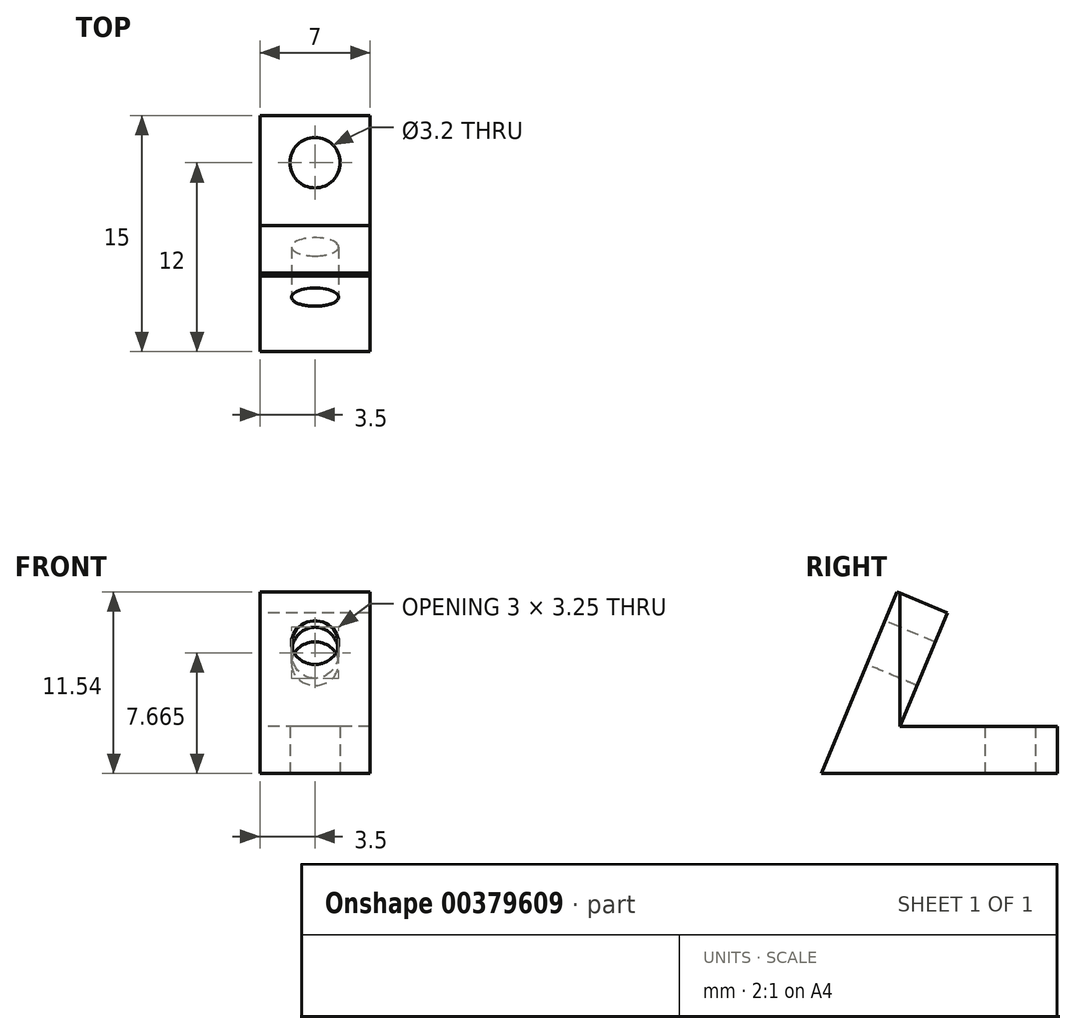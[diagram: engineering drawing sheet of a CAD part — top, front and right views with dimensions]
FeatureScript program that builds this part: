
annotation { "Feature Type Name" : "Feature", "Feature Type Description" : "" }
export const myFeature = defineFeature(function(context is Context, id is Id, definition is map)
    precondition{}
    {
        {
            var Q0;
            Q0=qCreatedBy(makeId("Top.planeOp"),FACE);
            var sketch = newSketch(context, id + "F0", { "sketchPlane" : qUnion([Q0])});
            skLineSegment(sketch, "E0.bottom", {"start": v(0, 0) * mm, "end": v(-7, 0) * mm});
            skLineSegment(sketch, "E0.top", {"start": v(0, -15) * mm, "end": v(-7, -15) * mm});
            skLineSegment(sketch, "E0.left", {"start": v(0, 0) * mm, "end": v(0, -15) * mm});
            skLineSegment(sketch, "E0.right", {"start": v(-7, 0) * mm, "end": v(-7, -15) * mm});
            skLineSegment(sketch, "E1", {"start": v(-7, -10) * mm, "end": v(0, -10) * mm});
            skPoint(sketch, "E2", {"position": v(-3.5, -3) * mm});
            skPoint(sketch, "E2.positionSnap0", {"position": v(-3.5, 0) * mm});
            skCircle(sketch, "E3", {"center": v(-3.5, -3) * mm, "radius": 1.6 * mm});
            skSolve(sketch);
        }
        {
            var Q0;
            {var subQ0=sQuery(id+"F0.wireOp",EDGE,"E0.bottom");Q0=makeQuery(id+"F0.imprint","IMPRINT",FACE,{"disambiguationData":[TD([[makeQuery(id+"F0.imprint","IMPRINT",EDGE,{"derivedFrom":subQ0}),1.0]])]});}
            extrude(context, id + "F1", {"entities" : qUnion([Q0]), "depth" : 3 * mm});
        }
        {
            var Q0;
            {var subQ0=sQuery(id+"F0.wireOp",EDGE,"E0.top");Q0=makeQuery(id+"F0.imprint","IMPRINT",FACE,{"disambiguationData":[TD([[makeQuery(id+"F0.imprint","IMPRINT",EDGE,{"derivedFrom":subQ0}),-1.0]])]});}
            extrude(context, id + "F2", {"entities" : qUnion([Q0]), "operationType" : NewBodyOperationType.ADD, "depth" : 12 * mm});
        }
        {
            var Q0;
            {var subQ0=sQuery(id+"F0.wireOp",EDGE,"E0.right");Q0=makeQuery(id+"F2.boolean.opBoolean","MERGE",FACE,{"derivedFrom":[makeQuery(id+"F1.opExtrude","SWEPT_FACE",FACE,{"disambiguationData":[OSD([subQ0])]}),makeQuery(id+"F2.opExtrude","SWEPT_FACE",FACE,{"disambiguationData":[OSD([subQ0])]})]});}
            var sketch = newSketch(context, id + "F3", { "sketchPlane" : qUnion([Q0])});
            skLineSegment(sketch, "E4", {"start": v(15, 0) * mm, "end": v(10, 12) * mm});
            skLineSegment(sketch, "E5", {"start": v(10, 3) * mm, "end": v(7, 10.2) * mm});
            skLineSegment(sketch, "E6", {"start": v(7, 10.2) * mm, "end": v(10.2, 11.54) * mm});
            skSolve(sketch);
        }
        {
            var Q0;
            {var subQ1=sQuery(id+"F0.wireOp",EDGE,"E0.right");var subQ4=makeQuery(id+"F2.opExtrude","CAP_EDGE",EDGE,{"disambiguationData":[OSD([subQ1])],"isStart":false});Q0=makeQuery(id+"F3.imprint","IMPRINT",FACE,{"disambiguationData":[TD([[makeQuery(id+"F3.imprint","IMPRINT",EDGE,{"derivedFrom":subQ4}),-1.0]])]});}
            var Q1;
            {var subQ0=sQuery(id+"F3.wireOp",EDGE,"E4");var subQ4=sQuery(id+"F3.wireOp",EDGE,"E6");var subQ5=makeQuery(id+"F3.imprint","INTERSECT",VERTEX,{"derivedFrom":[subQ0,subQ4]});Q1=makeQuery(id+"F3.imprint","IMPRINT",FACE,{"disambiguationData":[TD([[makeQuery(id+"F3.imprint","IMPRINT",EDGE,{"disambiguationData":[TD([[subQ5,1.0]])],"derivedFrom":subQ4}),1.0]])]});}
            extrude(context, id + "F4", {"entities" : qUnion([Q0, Q1]), "operationType" : NewBodyOperationType.REMOVE, "oppositeDirection" : true, "depth" : 25 * mm});
        }
        {
            var Q0;
            {var subQ0=sQuery(id+"F3.wireOp",EDGE,"E5");Q0=makeQuery(id+"F3.imprint","IMPRINT",FACE,{"disambiguationData":[TD([[makeQuery(id+"F3.imprint","IMPRINT",EDGE,{"derivedFrom":subQ0}),-1.0]])]});}
            extrude(context, id + "F5", {"entities" : qUnion([Q0]), "oppositeDirection" : true, "depth" : 7 * mm});
        }
        {
            var Q0;
            Q0=makeQuery(id+"F4.boolean.opBoolean","COPY",FACE,{"derivedFrom":makeQuery(id+"F4.opExtrude","SWEPT_FACE",FACE,{"disambiguationData":[OSD([sQuery(id+"F3.wireOp",EDGE,"E4")])]})});
            var sketch = newSketch(context, id + "F6", { "sketchPlane" : qUnion([Q0])});
            skPoint(sketch, "E7", {"position": v(-3.5, 3.23) * mm});
            skPoint(sketch, "E7.positionSnap0", {"position": v(-3.5, 6.73) * mm});
            skCircle(sketch, "E8", {"center": v(-3.5, 3.23) * mm, "radius": 1.5 * mm});
            skSolve(sketch);
        }
        {
            var Q0;
            Q0=makeQuery(id+"F6.imprint","IMPRINT",FACE,{"disambiguationData":[TD([[makeQuery(id+"F6.imprint","IMPRINT",EDGE,{"derivedFrom":sQuery(id+"F6.wireOp",EDGE,"E8")}),1.0]])]});
            extrude(context, id + "F7", {"entities" : qUnion([Q0]), "operationType" : NewBodyOperationType.REMOVE, "oppositeDirection" : true, "depth" : 10 * mm});
        }
    });
